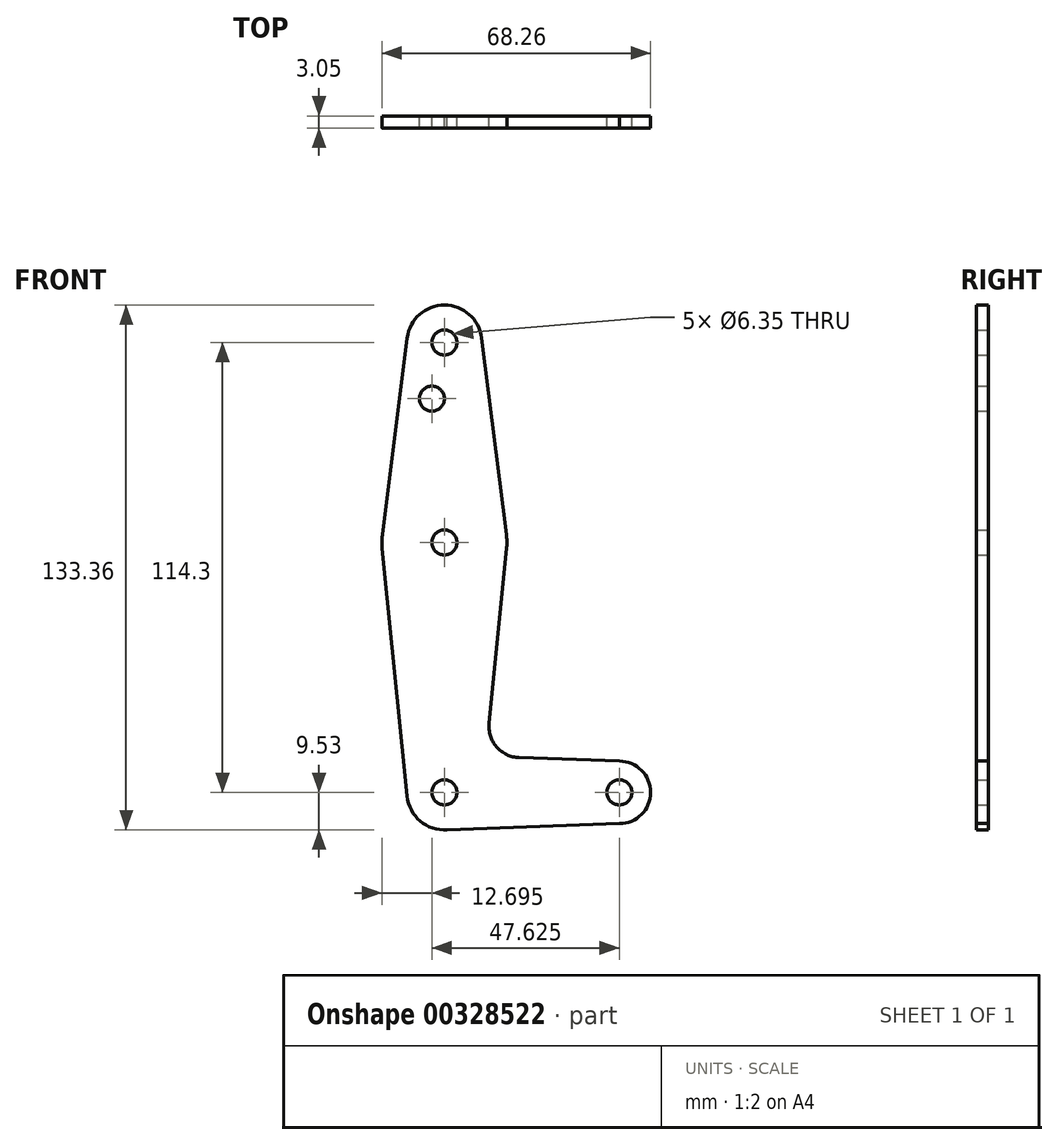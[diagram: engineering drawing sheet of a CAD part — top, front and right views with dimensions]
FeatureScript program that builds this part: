
annotation { "Feature Type Name" : "Feature", "Feature Type Description" : "" }
export const myFeature = defineFeature(function(context is Context, id is Id, definition is map)
    precondition{}
    {
        {
            var Q0;
            Q0=qCreatedBy(makeId("Front.planeOp"),FACE);
            var sketch = newSketch(context, id + "F0", { "sketchPlane" : qUnion([Q0])});
            skLineSegment(sketch, "E0", {"start": v(0, 0) * mm, "end": v(0, 114.3) * mm, "construction": true});
            skLineSegment(sketch, "E1", {"start": v(0, 0) * mm, "end": v(44.45, 0) * mm, "construction": true});
            skCircle(sketch, "E2", {"center": v(0, 114.3) * mm, "radius": 9.53 * mm});
            skCircle(sketch, "E3", {"center": v(0, 0) * mm, "radius": 9.53 * mm});
            skCircle(sketch, "E4", {"center": v(44.45, 0) * mm, "radius": 7.94 * mm});
            skCircle(sketch, "E5", {"center": v(0, 63.5) * mm, "radius": 15.88 * mm});
            skLineSegment(sketch, "E6", {"start": v(-9.45, 115.5) * mm, "end": v(-15.75, 65.48) * mm});
            skLineSegment(sketch, "E7", {"start": v(9.45, 115.5) * mm, "end": v(15.75, 65.48) * mm});
            skLineSegment(sketch, "E8", {"start": v(-15.8, 61.91) * mm, "end": v(-9.48, -0.95) * mm});
            skLineSegment(sketch, "E9", {"start": v(15.8, 61.91) * mm, "end": v(11.34, 17.59) * mm});
            skLineSegment(sketch, "E10", {"start": v(18.97, 8.85) * mm, "end": v(44.45, 7.94) * mm});
            skCircle(sketch, "E11", {"center": v(0, 114.3) * mm, "radius": 3.18 * mm});
            skCircle(sketch, "E12", {"center": v(0, 63.5) * mm, "radius": 3.18 * mm});
            skCircle(sketch, "E13", {"center": v(0, 0) * mm, "radius": 3.18 * mm});
            skCircle(sketch, "E14", {"center": v(44.45, 0) * mm, "radius": 3.18 * mm});
            skLineSegment(sketch, "E15", {"start": v(0, -9.52) * mm, "end": v(44.45, -7.94) * mm});
            skCircle(sketch, "E16", {"center": v(-3.18, 100.03) * mm, "radius": 3.18 * mm});
            skPoint(sketch, "E17.newPointB", {"position": v(0, 9.52) * mm});
            skArc(sketch, "E17.filletArc", {"start": v(11.34, 17.59) * mm, "mid": v(13.26, 11.57) * mm, "end": v(18.97, 8.85) * mm});
            skSolve(sketch);
        }
        {
            var Q0;
            Q0 = qSketchRegion(id + "F0", true);
            extrude(context, id + "F1", {"entities" : qUnion([Q0]), "depth" : 3.05 * mm});
        }
    });
